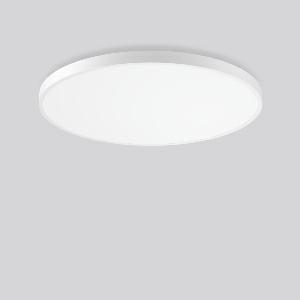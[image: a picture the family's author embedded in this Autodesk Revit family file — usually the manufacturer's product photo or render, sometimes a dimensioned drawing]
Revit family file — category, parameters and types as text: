
# Revit family: triona_round_a_312391_002_1_730_0b4f
name_source: partatom
category: Lighting Fixtures
units: mm (PartAtom-declared; Revit-internal decimal feet)

## family parameters
Cut with Voids When Loaded = No
Host = Face
Light Source = No
Part Type = Normal
Room Calculation Point = No
Round Connector Dimension = Use Diameter
Shared = No

## types (1)
- TRIONA round A (1 x LED Modul 840, 11700 lm, 4000)
    Apparent Load = 106 VA
    CIE Flux Codes = 49 80 96 100 100
    Color Rendering = 80
    Color Temperature = 4000
    Default Elevation = 1800 mm
    Description = Series: TRIONA round
Decorative round LED surface-mounted luminaire. Flat, seamless frame: aluminium extrusion profile, powder coated. Cover made of sheet steel, powder-coated. Light emission through a diffuser: plastic, opal. Lightguide and diffuser made of non-yellowing plastic (PMMA). Lateral light emission (RZB SIDELITE technology) for above-average homogeneous light distribution. Suitable for Ceiling mounting, Wall (surface). Tool-free mounting via bayonet connection. Electronic ballast included. Very easy installation thanks to Plug+Play connection. With Casambi smart+free Bluetooth control for wireless network and operation using Android / iOS devices, free app available for download. 
Colour: traffic white, matt (RAL 9016)
Diameter: 1009 mm
Height: 88 mm
Lamp: LED
Socket: without socket
Colour temperature: 4000K
Colour rendering index (CRI): 80
System power: 106 W
Rated luminous flux: 11700 lm
Luminous efficiency: 110 lm/W
Control gear: Dimmable Bluetooth converter
Protection class: I
Type of protection: IP 20
    Height = 88 mm
    Lamp = 1 x LED Modul 840
    Lamp Light Flux = 11700 lm
    Lamp count = 1
    Length = 1009 mm
    Lifetime = 50000 h
    Luminous efficacy = 110 lm/W
    Manufacturer = RZB
    ModVariant = No
    Model = 312391.002.1.730
    Mounting Place = Ceiling
    Mounting Type = Surface mounted
    Number of Poles = 1
    OnlyDefault = Yes
    Power Factor = 1
    Product Name = TRIONA round A
    Product group = Surface mounted modular luminaires
    ProductGroupID = 306
    Protection Class = Protection class I
    Protection Degree = IP 20
    RLX_Detail_Level = 1
    RLX_Emergency_Light_Flux = 0 lm
    RLX_Emergency_Type = 0
    RLX_Emergency_Type_DB = No
    RlxData = <blob elided: 36749 chars, md5=97f54ded>
    Socket = socket
    Standby Power = 0 W
    System Light Flux = 11700 lm
    System Power = 106 W
    Type Comments = Product without accessories
    Type Image = 312392.002.jpg
    URL = http://relux.com
    VarID = ---
    Voltage = 230 V
    Voltage Range = 220-240 V
    Weight = 0.00 kg
    Width = 0 mm  [stored 0 ft]

note: [stored X ft] marks values corroborated as IEEE doubles in the binary element streams (Revit-internal decimal feet)

## geometry (parser evidence)
native form markers: Blend x4, Sweep x10
no freeform markers — native parametric forms only
